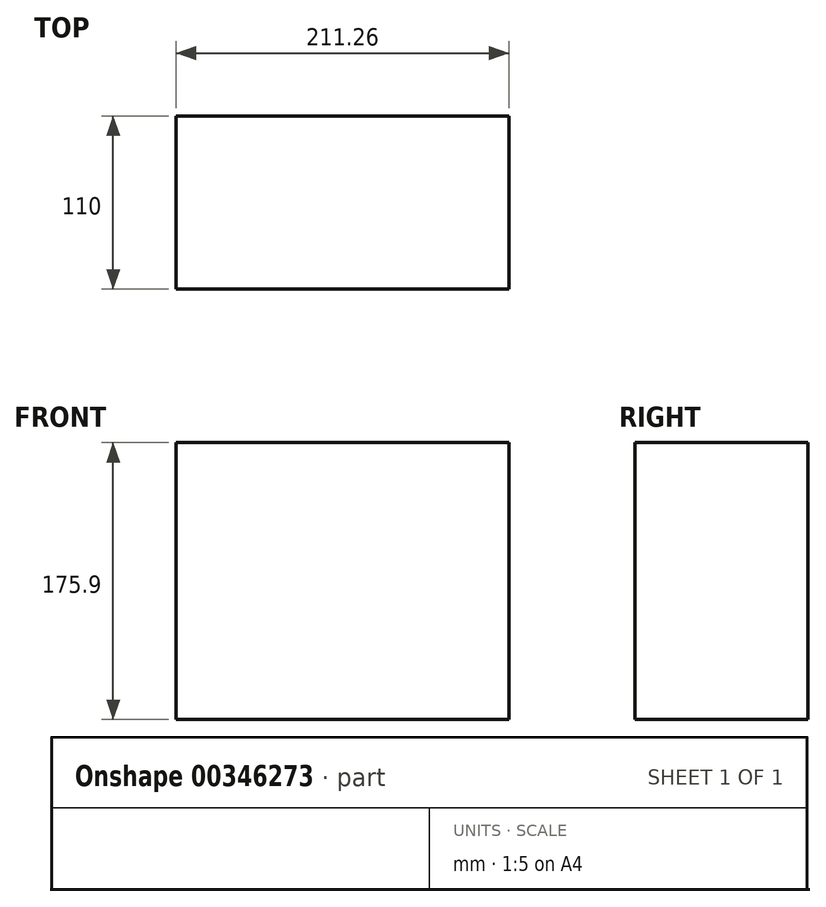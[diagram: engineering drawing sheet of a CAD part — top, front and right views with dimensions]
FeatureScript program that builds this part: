
annotation { "Feature Type Name" : "Feature", "Feature Type Description" : "" }
export const myFeature = defineFeature(function(context is Context, id is Id, definition is map)
    precondition{}
    {
        {
            var Q0;
            Q0=qCreatedBy(makeId("Front.planeOp"),FACE);
            var sketch = newSketch(context, id + "F0", { "sketchPlane" : qUnion([Q0])});
            skLineSegment(sketch, "E0.bottom", {"start": v(-105.59, 87.62) * mm, "end": v(105.67, 87.62) * mm});
            skLineSegment(sketch, "E0.top", {"start": v(-105.59, -88.28) * mm, "end": v(105.67, -88.28) * mm});
            skLineSegment(sketch, "E0.left", {"start": v(-105.59, 87.62) * mm, "end": v(-105.59, -88.28) * mm});
            skLineSegment(sketch, "E0.right", {"start": v(105.67, 87.62) * mm, "end": v(105.67, -88.28) * mm});
            skSolve(sketch);
        }
        {
            var Q0;
            Q0=makeQuery(id+"F0.imprint","IMPRINT",FACE,{"disambiguationData":[TD([[makeQuery(id+"F0.imprint","IMPRINT",EDGE,{"derivedFrom":sQuery(id+"F0.wireOp",EDGE,"E0.bottom")}),-1.0]])]});
            extrude(context, id + "F1", {"entities" : qUnion([Q0]), "depth" : 110 * mm});
        }
    });
